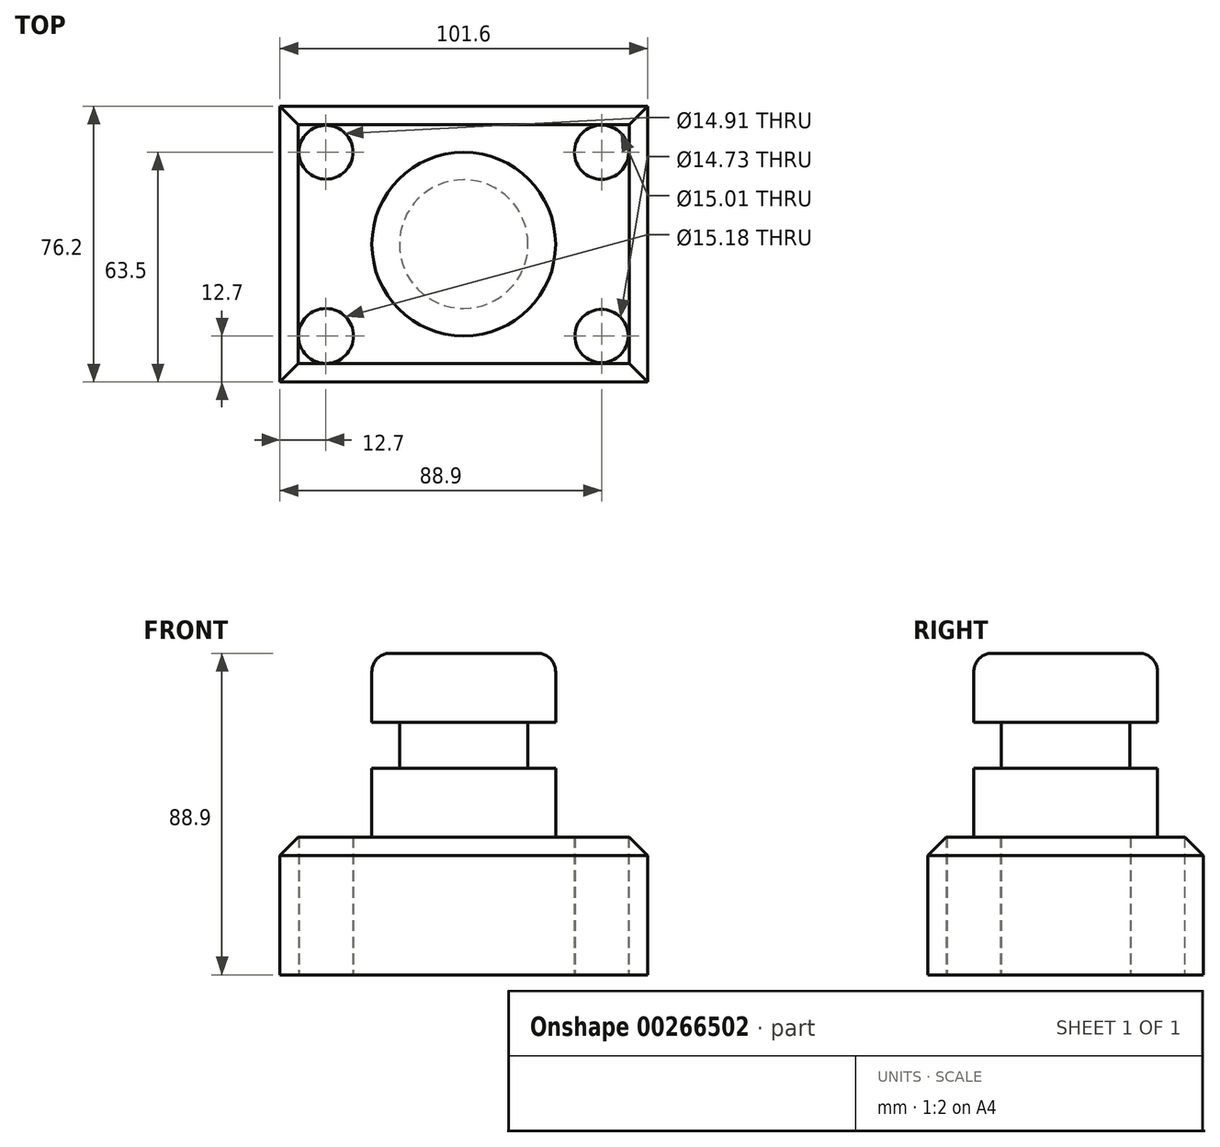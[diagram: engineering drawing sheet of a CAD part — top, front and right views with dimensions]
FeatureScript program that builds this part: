
annotation { "Feature Type Name" : "Feature", "Feature Type Description" : "" }
export const myFeature = defineFeature(function(context is Context, id is Id, definition is map)
    precondition{}
    {
        {
            var Q0;
            Q0=qCreatedBy(makeId("Top.planeOp"),FACE);
            var sketch = newSketch(context, id + "F0", { "sketchPlane" : qUnion([Q0])});
            skLineSegment(sketch, "E0.bottom", {"start": v(50.8, 38.1) * mm, "end": v(-50.8, 38.1) * mm});
            skLineSegment(sketch, "E0.top", {"start": v(50.8, -38.1) * mm, "end": v(-50.8, -38.1) * mm});
            skLineSegment(sketch, "E0.left", {"start": v(50.8, 38.1) * mm, "end": v(50.8, -38.1) * mm});
            skLineSegment(sketch, "E0.right", {"start": v(-50.8, 38.1) * mm, "end": v(-50.8, -38.1) * mm});
            skPoint(sketch, "E0.middle", {"position": v(0, 0) * mm});
            skSolve(sketch);
        }
        {
            var Q0;
            Q0=makeQuery(id+"F0.imprint","IMPRINT",FACE,{"disambiguationData":[TD([[makeQuery(id+"F0.imprint","IMPRINT",EDGE,{"derivedFrom":sQuery(id+"F0.wireOp",EDGE,"E0.bottom")}),1.0]])]});
            extrude(context, id + "F1", {"entities" : qUnion([Q0]), "depth" : 38.1 * mm});
        }
        {
            var Q0;
            Q0=qCreatedBy(makeId("Top.planeOp"),FACE);
            var sketch = newSketch(context, id + "F2", { "sketchPlane" : qUnion([Q0])});
            skCircle(sketch, "E1", {"center": v(-38.1, 25.4) * mm, "radius": 7.45 * mm});
            skCircle(sketch, "E2", {"center": v(-38.1, -25.4) * mm, "radius": 7.59 * mm});
            skCircle(sketch, "E3", {"center": v(38.1, 25.4) * mm, "radius": 7.5 * mm});
            skCircle(sketch, "E4", {"center": v(38.1, -25.4) * mm, "radius": 7.36 * mm});
            skSolve(sketch);
        }
        {
            var Q0;
            Q0 = qSketchRegion(id + "F2", true);
            extrude(context, id + "F3", {"entities" : qUnion([Q0]), "operationType" : NewBodyOperationType.REMOVE, "endBound" : BoundingType.THROUGH_ALL, "depth" : 25.4 * mm});
        }
        {
            var Q0;
            Q0=qCreatedBy(makeId("Front.planeOp"),FACE);
            var sketch = newSketch(context, id + "F4", { "sketchPlane" : qUnion([Q0])});
            skLineSegment(sketch, "E5.bottom", {"start": v(0, 38.1) * mm, "end": v(-25.4, 38.1) * mm});
            skLineSegment(sketch, "E5.top", {"start": v(0, 88.9) * mm, "end": v(-25.4, 88.9) * mm});
            skLineSegment(sketch, "E5.left", {"start": v(0, 38.1) * mm, "end": v(0, 88.9) * mm});
            skLineSegment(sketch, "E5.right", {"start": v(-25.4, 38.1) * mm, "end": v(-25.4, 88.9) * mm});
            skSolve(sketch);
        }
        {
            var Q0;
            Q0=makeQuery(id+"F4.imprint","IMPRINT",FACE,{"disambiguationData":[TD([[makeQuery(id+"F4.imprint","IMPRINT",EDGE,{"derivedFrom":sQuery(id+"F4.wireOp",EDGE,"E5.bottom")}),-1.0]])]});
            var Q1;
            Q1=sQuery(id+"F4.wireOp",EDGE,"E5.left");
            revolve(context, id + "F5", {"operationType" : NewBodyOperationType.ADD, "entities" : qUnion([Q0]), "axis" : qUnion([Q1]), "revolveType" : RevolveType.FULL, "oppositeDirection" : true});
        }
        {
            var Q0;
            Q0=qCreatedBy(makeId("Front.planeOp"),FACE);
            var sketch = newSketch(context, id + "F6", { "sketchPlane" : qUnion([Q0])});
            skLineSegment(sketch, "E6.bottom", {"start": v(-30.48, 69.85) * mm, "end": v(-17.78, 69.85) * mm});
            skLineSegment(sketch, "E6.top", {"start": v(-30.48, 57.15) * mm, "end": v(-17.78, 57.15) * mm});
            skLineSegment(sketch, "E6.left", {"start": v(-30.48, 69.85) * mm, "end": v(-30.48, 57.15) * mm});
            skLineSegment(sketch, "E6.right", {"start": v(-17.78, 69.85) * mm, "end": v(-17.78, 57.15) * mm});
            skSolve(sketch);
        }
        {
            var Q0;
            Q0=makeQuery(id+"F6.imprint","IMPRINT",FACE,{"disambiguationData":[TD([[makeQuery(id+"F6.imprint","IMPRINT",EDGE,{"derivedFrom":sQuery(id+"F6.wireOp",EDGE,"E6.bottom")}),-1.0]])]});
            var Q1;
            Q1=makeQuery(id+"F5.opRevolve","SWEPT_FACE",FACE,{"disambiguationData":[OSD([sQuery(id+"F4.wireOp",EDGE,"E5.right")])]});
            revolve(context, id + "F7", {"operationType" : NewBodyOperationType.REMOVE, "entities" : qUnion([Q0]), "axis" : qUnion([Q1]), "revolveType" : RevolveType.FULL, "oppositeDirection" : true});
        }
        {
            var Q0;
            Q0=makeQuery(id+"F5.opRevolve","SWEPT_EDGE",EDGE,{"disambiguationData":[OSD([sQuery(id+"F4.wireOp",EDGE,"E5.top"),sQuery(id+"F4.wireOp",EDGE,"E5.right")])]});
            var Q1;
            Q1=makeQuery(id+"F5.opRevolve","SWEPT_EDGE",EDGE,{"disambiguationData":[OSD([sQuery(id+"F4.wireOp",EDGE,"E5.bottom"),sQuery(id+"F4.wireOp",EDGE,"E5.right")])]});
            fillet(context, id + "F8", {"entities" : qUnion([Q0, Q1]), "radius" : 5.08 * mm, "tangentPropagation" : true, "allowEdgeOverflow" : false});
        }
        {
            var Q0;
            Q0=makeQuery(id+"F1.opExtrude","CAP_EDGE",EDGE,{"disambiguationData":[OSD([sQuery(id+"F0.wireOp",EDGE,"E0.top")])],"isStart":false});
            var Q1;
            Q1=makeQuery(id+"F1.opExtrude","CAP_EDGE",EDGE,{"disambiguationData":[OSD([sQuery(id+"F0.wireOp",EDGE,"E0.left")])],"isStart":false});
            var Q2;
            Q2=makeQuery(id+"F1.opExtrude","CAP_EDGE",EDGE,{"disambiguationData":[OSD([sQuery(id+"F0.wireOp",EDGE,"E0.bottom")])],"isStart":false});
            var Q3;
            Q3=makeQuery(id+"F1.opExtrude","CAP_EDGE",EDGE,{"disambiguationData":[OSD([sQuery(id+"F0.wireOp",EDGE,"E0.right")])],"isStart":false});
            chamfer(context, id + "F9", {"entities" : qUnion([Q0, Q1, Q2, Q3]), "width" : 5.08 * mm, "tangentPropagation" : true});
        }
    });
